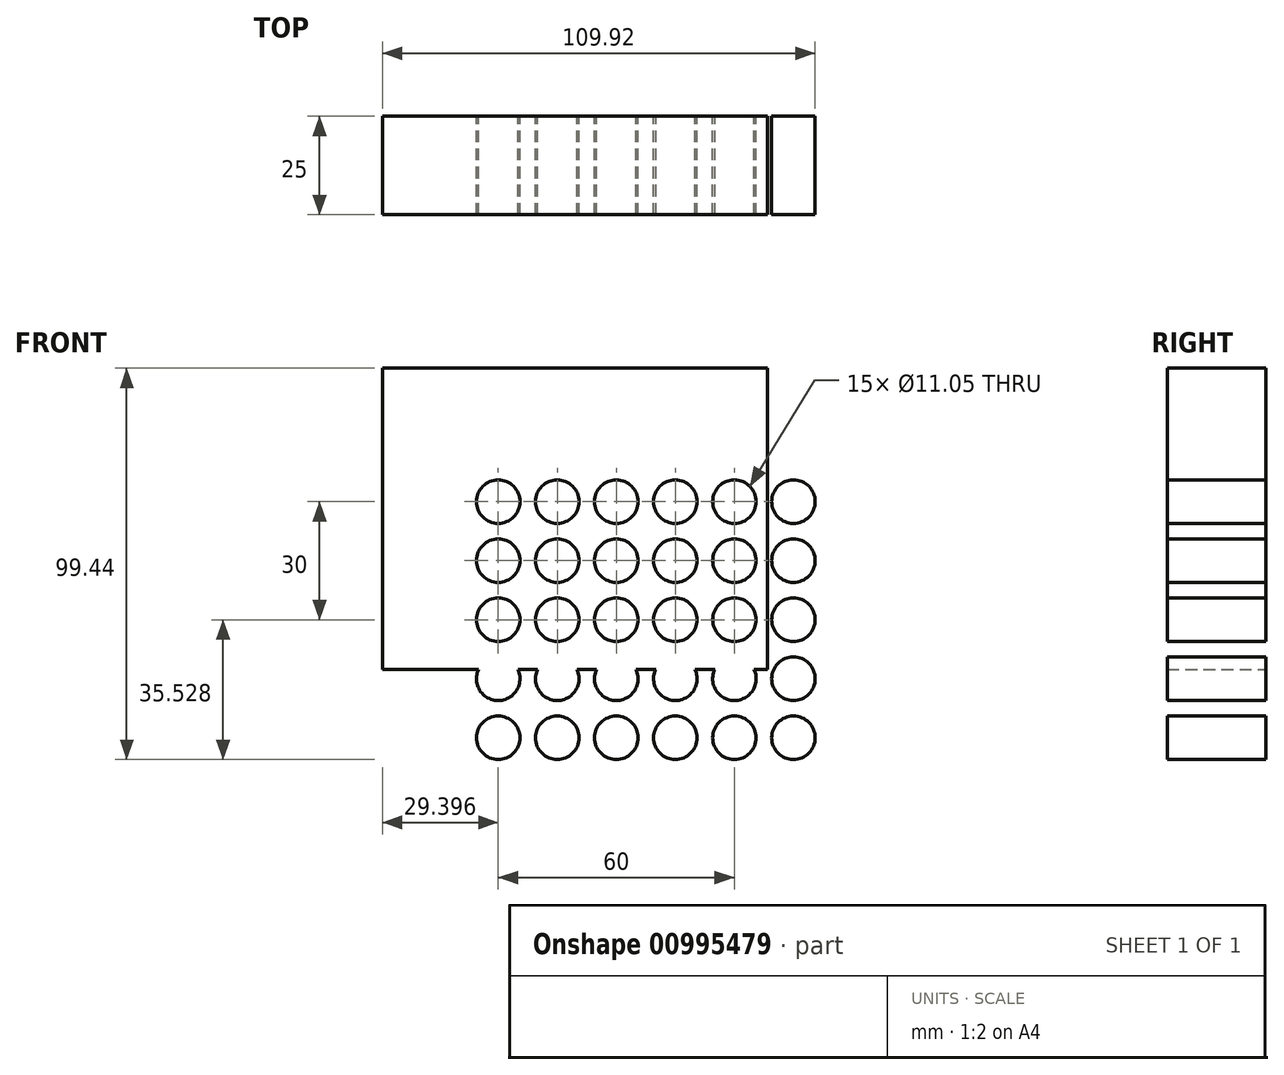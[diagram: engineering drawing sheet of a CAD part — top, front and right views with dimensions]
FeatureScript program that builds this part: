
annotation { "Feature Type Name" : "Feature", "Feature Type Description" : "" }
export const myFeature = defineFeature(function(context is Context, id is Id, definition is map)
    precondition{}
    {
        {
            var Q0;
            Q0=qCreatedBy(makeId("Front.planeOp"),FACE);
            var sketch = newSketch(context, id + "F0", { "sketchPlane" : qUnion([Q0])});
            skLineSegment(sketch, "E0.bottom", {"start": v(-49.97, 36.77) * mm, "end": v(47.82, 36.77) * mm});
            skLineSegment(sketch, "E0.top", {"start": v(-49.97, -39.74) * mm, "end": v(47.82, -39.74) * mm});
            skLineSegment(sketch, "E0.left", {"start": v(-49.97, 36.77) * mm, "end": v(-49.97, -39.74) * mm});
            skLineSegment(sketch, "E0.right", {"start": v(47.82, 36.77) * mm, "end": v(47.82, -39.74) * mm});
            skCircle(sketch, "E1", {"center": v(-20.57, 2.86) * mm, "radius": 5.53 * mm});
            skCircle(sketch, "E2.0.1.0", {"center": v(-20.57, -12.14) * mm, "radius": 5.53 * mm});
            skCircle(sketch, "E2.0.2.0", {"center": v(-20.57, -27.14) * mm, "radius": 5.53 * mm});
            skCircle(sketch, "E2.0.3.0", {"center": v(-20.57, -42.14) * mm, "radius": 5.53 * mm});
            skCircle(sketch, "E2.0.4.0", {"center": v(-20.57, -57.14) * mm, "radius": 5.53 * mm});
            skCircle(sketch, "E2.1.0.0", {"center": v(-5.57, 2.86) * mm, "radius": 5.53 * mm});
            skCircle(sketch, "E2.1.1.0", {"center": v(-5.57, -12.14) * mm, "radius": 5.53 * mm});
            skCircle(sketch, "E2.1.2.0", {"center": v(-5.57, -27.14) * mm, "radius": 5.53 * mm});
            skCircle(sketch, "E2.1.3.0", {"center": v(-5.57, -42.14) * mm, "radius": 5.53 * mm});
            skCircle(sketch, "E2.1.4.0", {"center": v(-5.57, -57.14) * mm, "radius": 5.53 * mm});
            skCircle(sketch, "E2.2.0.0", {"center": v(9.43, 2.86) * mm, "radius": 5.53 * mm});
            skCircle(sketch, "E2.2.1.0", {"center": v(9.43, -12.14) * mm, "radius": 5.53 * mm});
            skCircle(sketch, "E2.2.2.0", {"center": v(9.43, -27.14) * mm, "radius": 5.53 * mm});
            skCircle(sketch, "E2.2.3.0", {"center": v(9.43, -42.14) * mm, "radius": 5.53 * mm});
            skCircle(sketch, "E2.2.4.0", {"center": v(9.43, -57.14) * mm, "radius": 5.53 * mm});
            skCircle(sketch, "E2.3.0.0", {"center": v(24.43, 2.86) * mm, "radius": 5.53 * mm});
            skCircle(sketch, "E2.3.1.0", {"center": v(24.43, -12.14) * mm, "radius": 5.53 * mm});
            skCircle(sketch, "E2.3.2.0", {"center": v(24.43, -27.14) * mm, "radius": 5.53 * mm});
            skCircle(sketch, "E2.3.3.0", {"center": v(24.43, -42.14) * mm, "radius": 5.53 * mm});
            skCircle(sketch, "E2.3.4.0", {"center": v(24.43, -57.14) * mm, "radius": 5.53 * mm});
            skCircle(sketch, "E2.4.0.0", {"center": v(39.43, 2.86) * mm, "radius": 5.53 * mm});
            skCircle(sketch, "E2.4.1.0", {"center": v(39.43, -12.14) * mm, "radius": 5.53 * mm});
            skCircle(sketch, "E2.4.2.0", {"center": v(39.43, -27.14) * mm, "radius": 5.53 * mm});
            skCircle(sketch, "E2.4.3.0", {"center": v(39.43, -42.14) * mm, "radius": 5.53 * mm});
            skCircle(sketch, "E2.4.4.0", {"center": v(39.43, -57.14) * mm, "radius": 5.53 * mm});
            skLineSegment(sketch, "E2.direction1", {"start": v(-20.57, 2.86) * mm, "end": v(-5.57, 2.86) * mm, "construction": true});
            skLineSegment(sketch, "E2.direction2", {"start": v(-20.57, 2.86) * mm, "end": v(-20.57, -12.14) * mm, "construction": true});
            skCircle(sketch, "E3.0.5.0", {"center": v(54.43, 2.86) * mm, "radius": 5.53 * mm});
            skCircle(sketch, "E3.0.5.1", {"center": v(54.43, -12.14) * mm, "radius": 5.53 * mm});
            skCircle(sketch, "E3.0.5.2", {"center": v(54.43, -27.14) * mm, "radius": 5.53 * mm});
            skCircle(sketch, "E3.0.5.3", {"center": v(54.43, -42.14) * mm, "radius": 5.53 * mm});
            skCircle(sketch, "E3.0.5.4", {"center": v(54.43, -57.14) * mm, "radius": 5.53 * mm});
            skSolve(sketch);
        }
        {
            var Q0;
            Q0 = qSketchRegion(id + "F0", true);
            extrude(context, id + "F1", {"entities" : qUnion([Q0]), "depth" : 25 * mm, "offsetDistance" : 25 * mm});
        }
    });
